# Revit family: wd-240dk2(-rc)_60Hz
name_source: partatom
category: 機械設備
units: mm (PartAtom-declared; Revit-internal decimal feet)

## family parameters
OmniClass タイトル = Centrifugal Fans
OmniClass 番号 = 23.75.35.17.27
パーツ タイプ = 標準
ロード時にボイドで切り取り = いいえ
丸型コネクタ寸法 = 直径を使用
作業面ベース = いいえ
共有 = いいえ
常に垂直 = はい
部屋計算ポイント = いいえ

## types (2) — shared parameters
Clearance Bottom = 100  [stored 0.328084 ft]
Clearance Front = 100  [stored 0.328084 ft]
Clearance Left = 50
Clearance Right = 50
Clearance Top = 50
D1 = 135
Depth = 175  [stored 0.574147 ft]
H1 = 106
Height = 280
IfcExportAs = IfcFanType
IfcExportType = PROPELLORAXIAL
MAX静圧 = 0.0 Pa
MAX風量 = 195.0 m³/h
MID静圧 = 0.0 Pa
MID風量 = 195.0 m³/h
MIN静圧 = 0.0 Pa
MIN風量 = 100.0 m³/h
OmniClassCode = 23-33 31 19 11 15
URL = https://www.mitsubishielectric.co.jp
Uniclass2015Code = Pr_65_67_29_12
Uniclass2015Title = Centrifugal fans
Uniclass2015Version = Systems v1.9
W1 = 122
Width = 498  [stored 1.63386 ft]
マテリアル = 合成樹脂(白)
メンテナンススペース = はい
仕様書バージョン = Version1.0
企業コード = 108420
分類コード = 50052503100080
周波数 = 60 Hz
極数 = 3
法定耐用年数 = 10
消費電力 = 2310 W
相 = 1
積算_科目 = 2 換気設備
製品リリース年月 = 2022年6月1日
製品出荷対象 = 国内
製品質量 = 7.40 kg
製造元 = 三菱電機株式会社
設置方法 = 壁付
説明 = バス乾燥・暖房・換気システム 脱衣室暖房機
負荷分類 = 3_ファン類
質量 = 8.88 kg
運転質量 = 0.00 kg
電動機出力 = 0 W
電圧 = 200 V
zero-valued in all types: Clearance Back

## per-type parameters (varying)
| type | 価格 |
| WD-240DK2 | 132600 $ |
| WD-240DK2-RC | 164900 $ |

note: column(s) folded — value = type name in every type: モデル

note: [stored X ft] marks values corroborated as IEEE doubles in the binary element streams (Revit-internal decimal feet)
